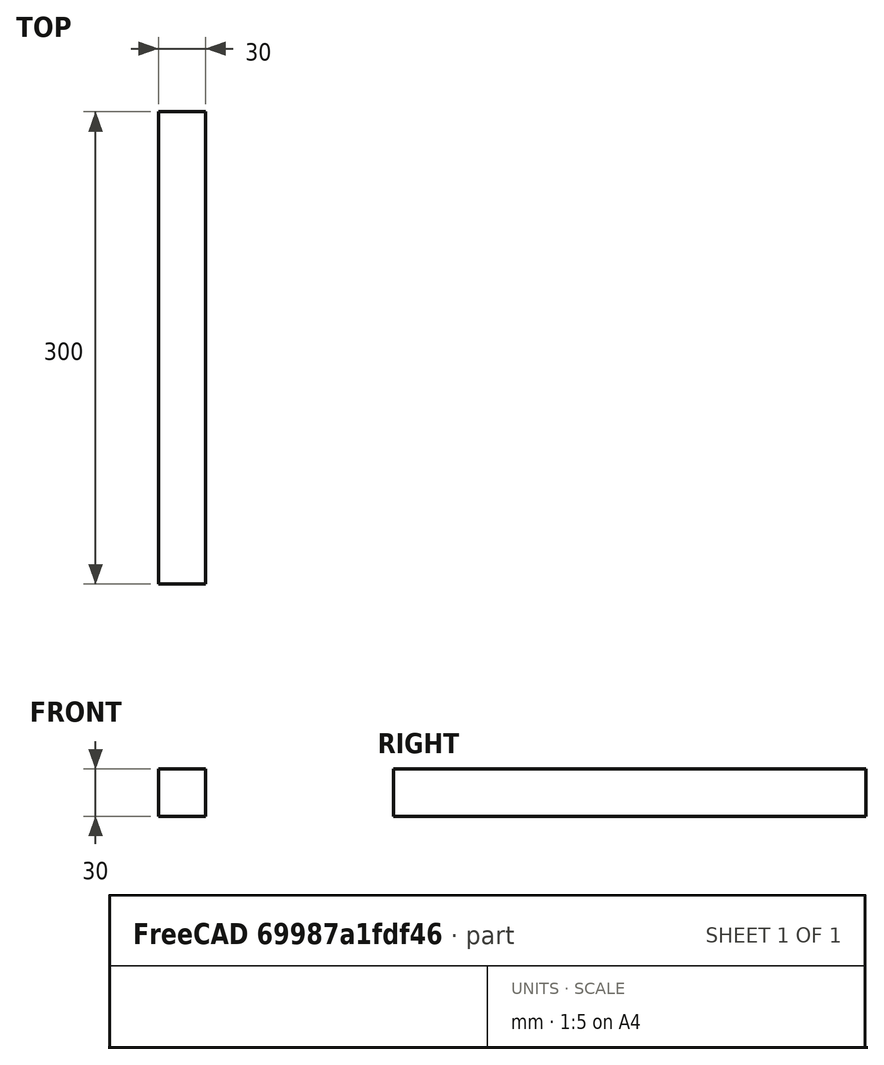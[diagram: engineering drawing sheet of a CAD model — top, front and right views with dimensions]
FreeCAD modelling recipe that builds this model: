
FCSTD DOCUMENT  (FreeCAD 0.20R29177 (Git))
Label: handlebartop
License: All rights reserved
LicenseURL: http://en.wikipedia.org/wiki/All_rights_reserved
objects: Sketcher::SketchObject×1, PartDesign::Pad×1, PartDesign::Body×1
note: 4 computed .brp shape members not serialized (recipe doc carries the construction recipe); baked Part::Feature solids carry a one-line shape summary decoded from their .brp

FEATURE [Sketcher::SketchObject] Sketch
  FullyConstrained = true
  MapMode = 5
  Placement = pos=(0,0,0) rot=(1,0,0;1.5708rad)
  Support = -> [XZ_Plane]
  sketch-geometry (4):
    g0: LineSegment StartX=0 StartY=0 StartZ=0 EndX=30 EndY=0 EndZ=0
    g1: LineSegment StartX=30 StartY=0 StartZ=0 EndX=30 EndY=30 EndZ=0
    g2: LineSegment StartX=30 StartY=30 StartZ=0 EndX=0 EndY=30 EndZ=0
    g3: LineSegment StartX=0 StartY=30 StartZ=0 EndX=0 EndY=0 EndZ=0
  constraints (11):
    c: Coincident(g0,g1)
    c: Coincident(g1,g2)
    c: Coincident(g2,g3)
    c: Coincident(g3,g0)
    c: Horizontal(g0)
    c: Horizontal(g2)
    c: Vertical(g1)
    c: Vertical(g3)
    c: Coincident(g0,g-1)
    c: DistanceX(g2,g2) = 30
    c: DistanceY(g1,g1) = 30
FEATURE [PartDesign::Pad] Pad
  Direction = (1,1,1)
  Length = 300
  Length2 = 100
  Placement = pos=(0,0,0) rot=(1,0,0;1.5708rad)
  Profile = -> Sketch
  Type = 0
FEATURE [PartDesign::Body] Body  label="hanndlebartop"
  Group = -> [Sketch,Pad]
  Origin = -> Origin
  Tip = -> Pad
